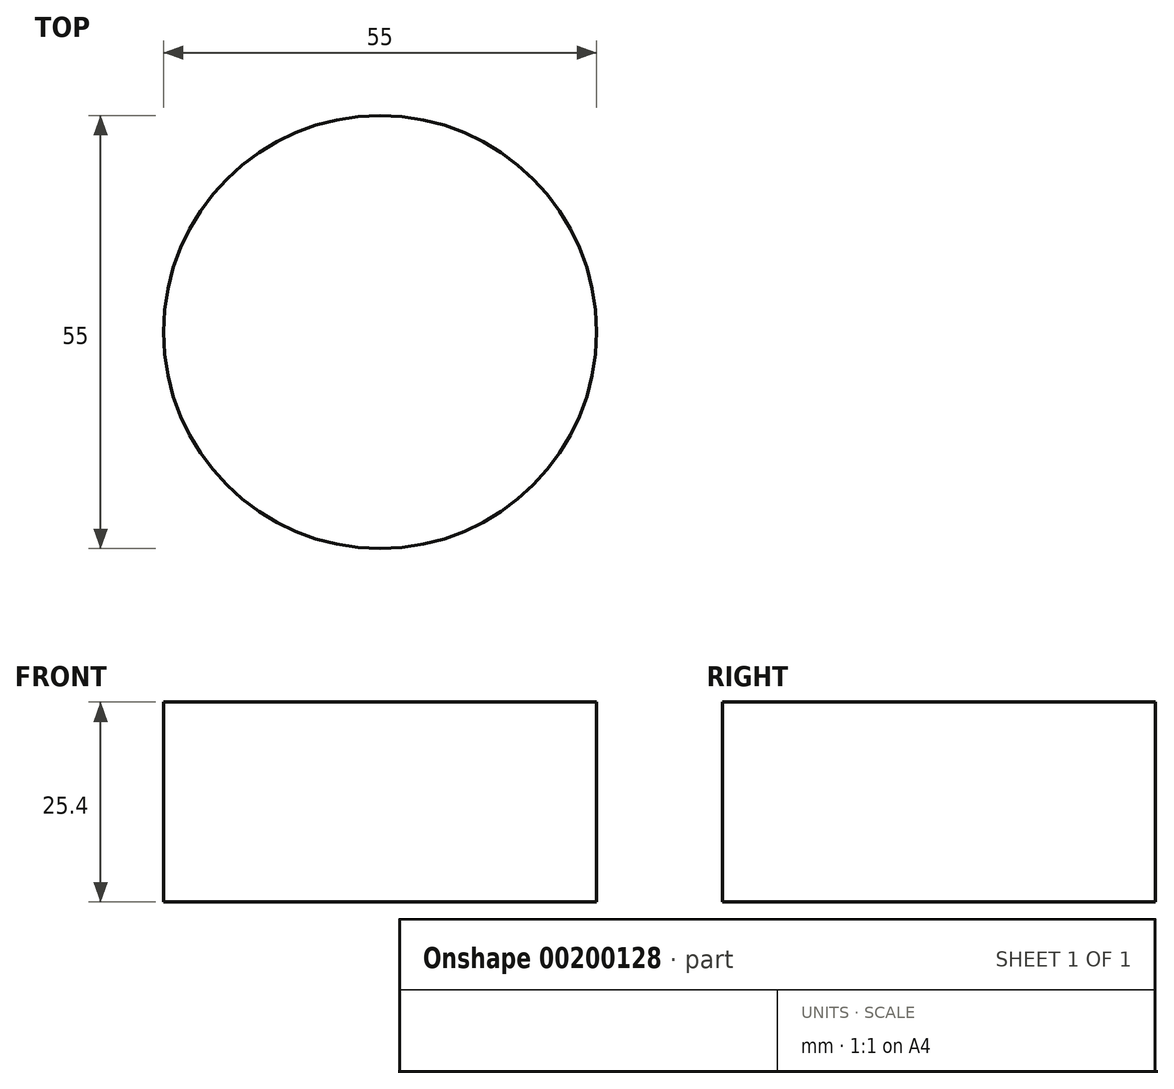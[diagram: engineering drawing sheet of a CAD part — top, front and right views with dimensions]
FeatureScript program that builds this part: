
annotation { "Feature Type Name" : "Feature", "Feature Type Description" : "" }
export const myFeature = defineFeature(function(context is Context, id is Id, definition is map)
    precondition{}
    {
        {
            var Q0;
            Q0=qCreatedBy(makeId("Top.planeOp"),FACE);
            var sketch = newSketch(context, id + "F0", { "sketchPlane" : qUnion([Q0])});
            skCircle(sketch, "E0", {"center": v(0, 25.9) * mm, "radius": 21.49 * mm});
            skCircle(sketch, "E1", {"center": v(0, 25.9) * mm, "radius": 27.5 * mm});
            skSolve(sketch);
        }
        {
            var Q0;
            Q0=makeQuery(id+"F0.imprint","IMPRINT",FACE,{"disambiguationData":[TD([[makeQuery(id+"F0.imprint","IMPRINT",EDGE,{"derivedFrom":sQuery(id+"F0.wireOp",EDGE,"E0")}),1.0]])]});
            var Q1;
            Q1=makeQuery(id+"F0.imprint","IMPRINT",FACE,{"disambiguationData":[TD([[makeQuery(id+"F0.imprint","IMPRINT",EDGE,{"derivedFrom":sQuery(id+"F0.wireOp",EDGE,"E0")}),-1.0]])]});
            extrude(context, id + "F1", {"entities" : qUnion([Q0, Q1]), "depth" : 25.4 * mm});
        }
    });
